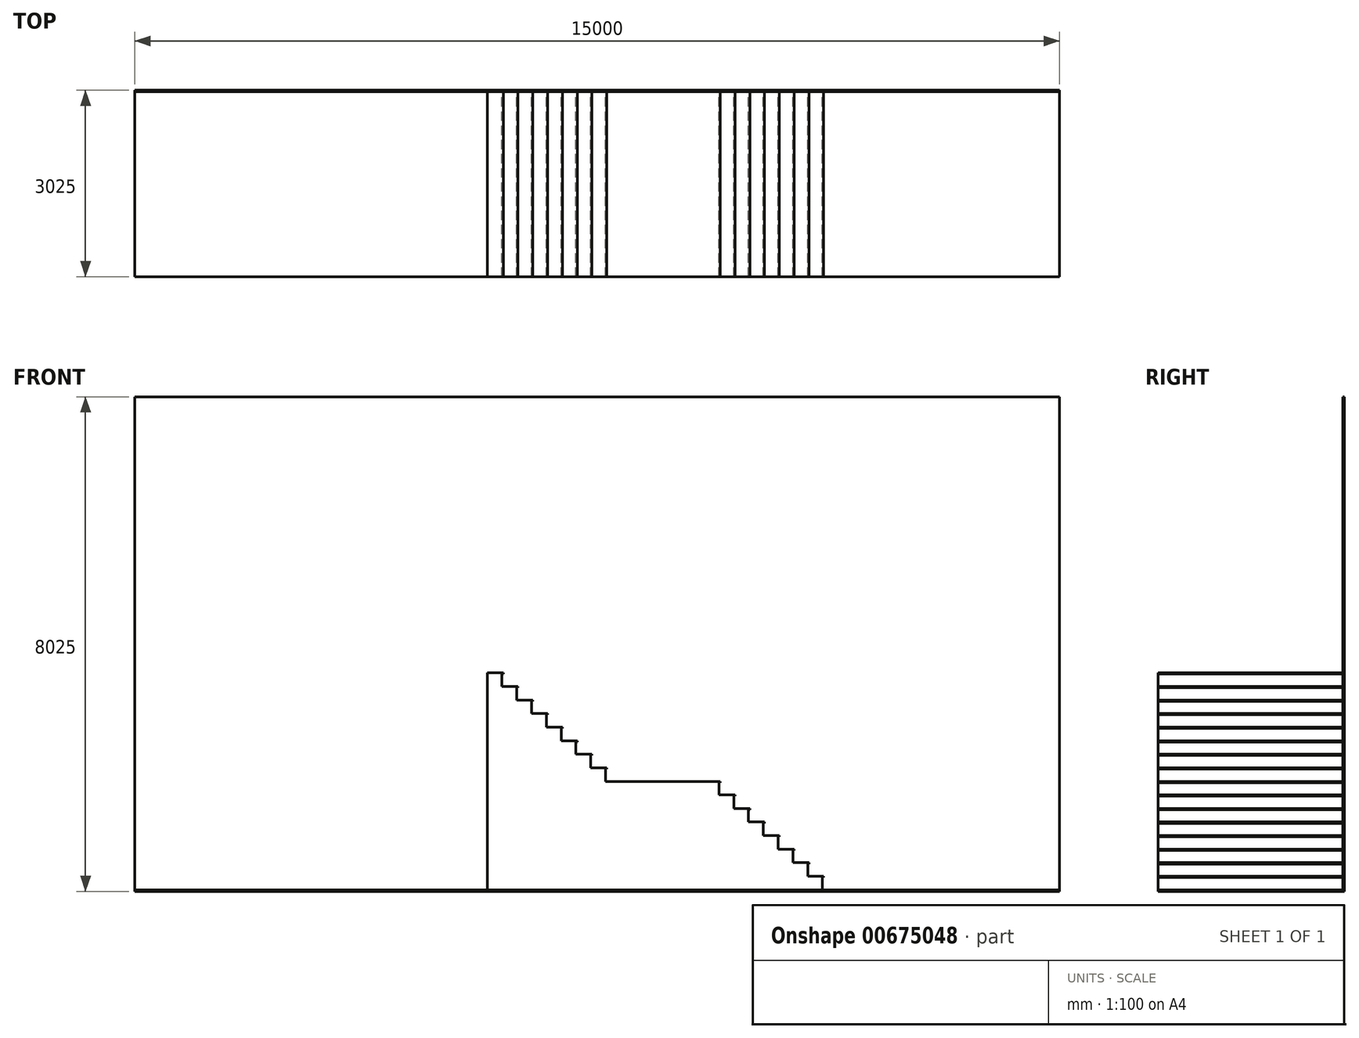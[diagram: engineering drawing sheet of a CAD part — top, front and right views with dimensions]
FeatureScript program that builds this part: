
annotation { "Feature Type Name" : "Feature", "Feature Type Description" : "" }
export const myFeature = defineFeature(function(context is Context, id is Id, definition is map)
    precondition{}
    {
        {
            var Q0;
            Q0=qCreatedBy(makeId("Front.planeOp"),FACE);
            var sketch = newSketch(context, id + "F0", { "sketchPlane" : qUnion([Q0])});
            skLineSegment(sketch, "E0", {"start": v(0, 0) * mm, "end": v(260, 0) * mm});
            skLineSegment(sketch, "E1", {"start": v(260, 0) * mm, "end": v(260, -20) * mm});
            skLineSegment(sketch, "E2", {"start": v(260, -20) * mm, "end": v(240, -20) * mm});
            skLineSegment(sketch, "E3", {"start": v(240, -20) * mm, "end": v(240, -220) * mm});
            skPoint(sketch, "E4.orphan", {"position": v(260, -220) * mm});
            skLineSegment(sketch, "E5", {"start": v(0, 0) * mm, "end": v(240, -220) * mm, "construction": true});
            skLineSegment(sketch, "E6", {"start": v(240, -220) * mm, "end": v(500, -220) * mm});
            skLineSegment(sketch, "E7", {"start": v(500, -220) * mm, "end": v(500, -240) * mm});
            skLineSegment(sketch, "E8", {"start": v(500, -240) * mm, "end": v(480, -240) * mm});
            skLineSegment(sketch, "E9", {"start": v(480, -240) * mm, "end": v(480, -440) * mm});
            skPoint(sketch, "E10.orphan", {"position": v(500, -440) * mm});
            skLineSegment(sketch, "E11", {"start": v(240, -220) * mm, "end": v(480, -440) * mm, "construction": true});
            skLineSegment(sketch, "E12", {"start": v(480, -440) * mm, "end": v(740, -440) * mm});
            skLineSegment(sketch, "E13", {"start": v(740, -440) * mm, "end": v(740, -460) * mm});
            skLineSegment(sketch, "E14", {"start": v(740, -460) * mm, "end": v(720, -460) * mm});
            skLineSegment(sketch, "E15", {"start": v(720, -460) * mm, "end": v(720, -660) * mm});
            skPoint(sketch, "E16.orphan", {"position": v(740, -660) * mm});
            skLineSegment(sketch, "E17", {"start": v(480, -440) * mm, "end": v(720, -660) * mm, "construction": true});
            skLineSegment(sketch, "E18", {"start": v(720, -660) * mm, "end": v(980, -660) * mm});
            skLineSegment(sketch, "E19", {"start": v(980, -660) * mm, "end": v(980, -680) * mm});
            skLineSegment(sketch, "E20", {"start": v(980, -680) * mm, "end": v(960, -680) * mm});
            skLineSegment(sketch, "E21", {"start": v(960, -680) * mm, "end": v(960, -880) * mm});
            skPoint(sketch, "E22.orphan", {"position": v(980, -880) * mm});
            skLineSegment(sketch, "E23", {"start": v(720, -660) * mm, "end": v(960, -880) * mm, "construction": true});
            skLineSegment(sketch, "E24", {"start": v(960, -880) * mm, "end": v(1220, -880) * mm});
            skLineSegment(sketch, "E25", {"start": v(1220, -880) * mm, "end": v(1220, -900) * mm});
            skLineSegment(sketch, "E26", {"start": v(1220, -900) * mm, "end": v(1200, -900) * mm});
            skLineSegment(sketch, "E27", {"start": v(1200, -900) * mm, "end": v(1200, -1100) * mm});
            skPoint(sketch, "E28.orphan", {"position": v(1220, -1100) * mm});
            skLineSegment(sketch, "E29", {"start": v(960, -880) * mm, "end": v(1200, -1100) * mm, "construction": true});
            skLineSegment(sketch, "E30", {"start": v(1200, -1100) * mm, "end": v(1460, -1100) * mm});
            skLineSegment(sketch, "E31", {"start": v(1460, -1100) * mm, "end": v(1460, -1120) * mm});
            skLineSegment(sketch, "E32", {"start": v(1460, -1120) * mm, "end": v(1440, -1120) * mm});
            skLineSegment(sketch, "E33", {"start": v(1440, -1120) * mm, "end": v(1440, -1320) * mm});
            skPoint(sketch, "E34.orphan", {"position": v(1460, -1320) * mm});
            skLineSegment(sketch, "E35", {"start": v(1200, -1100) * mm, "end": v(1440, -1320) * mm, "construction": true});
            skLineSegment(sketch, "E36", {"start": v(1440, -1320) * mm, "end": v(1700, -1320) * mm});
            skLineSegment(sketch, "E37", {"start": v(1700, -1320) * mm, "end": v(1700, -1340) * mm});
            skLineSegment(sketch, "E38", {"start": v(1700, -1340) * mm, "end": v(1680, -1340) * mm});
            skLineSegment(sketch, "E39", {"start": v(1680, -1340) * mm, "end": v(1680, -1540) * mm});
            skPoint(sketch, "E40.orphan", {"position": v(1700, -1540) * mm});
            skLineSegment(sketch, "E41", {"start": v(1440, -1320) * mm, "end": v(1680, -1540) * mm, "construction": true});
            skLineSegment(sketch, "E42", {"start": v(1680, -1540) * mm, "end": v(1940, -1540) * mm});
            skLineSegment(sketch, "E43", {"start": v(1940, -1540) * mm, "end": v(1940, -1560) * mm});
            skLineSegment(sketch, "E44", {"start": v(1940, -1560) * mm, "end": v(1920, -1560) * mm});
            skLineSegment(sketch, "E45", {"start": v(1920, -1560) * mm, "end": v(1920, -1760) * mm});
            skPoint(sketch, "E46.orphan", {"position": v(1940, -1760) * mm});
            skLineSegment(sketch, "E47", {"start": v(1680, -1540) * mm, "end": v(1920, -1760) * mm, "construction": true});
            skLineSegment(sketch, "E48", {"start": v(1920, -1760) * mm, "end": v(3520, -1760) * mm});
            skLineSegment(sketch, "E49", {"start": v(3520, -1760) * mm, "end": v(3780, -1760) * mm});
            skLineSegment(sketch, "E50", {"start": v(3780, -1760) * mm, "end": v(3780, -1780) * mm});
            skLineSegment(sketch, "E51", {"start": v(3780, -1780) * mm, "end": v(3760, -1780) * mm});
            skLineSegment(sketch, "E52", {"start": v(3760, -1780) * mm, "end": v(3760, -1980) * mm});
            skPoint(sketch, "E53.orphan", {"position": v(3780, -1980) * mm});
            skLineSegment(sketch, "E54", {"start": v(3520, -1760) * mm, "end": v(3760, -1980) * mm, "construction": true});
            skLineSegment(sketch, "E55", {"start": v(3760, -1980) * mm, "end": v(4020, -1980) * mm});
            skLineSegment(sketch, "E56", {"start": v(4020, -1980) * mm, "end": v(4020, -2000) * mm});
            skLineSegment(sketch, "E57", {"start": v(4020, -2000) * mm, "end": v(4000, -2000) * mm});
            skLineSegment(sketch, "E58", {"start": v(4000, -2000) * mm, "end": v(4000, -2200) * mm});
            skPoint(sketch, "E59.orphan", {"position": v(4020, -2200) * mm});
            skLineSegment(sketch, "E60", {"start": v(3760, -1980) * mm, "end": v(4000, -2200) * mm, "construction": true});
            skLineSegment(sketch, "E61", {"start": v(4000, -2200) * mm, "end": v(4260, -2200) * mm});
            skLineSegment(sketch, "E62", {"start": v(4260, -2200) * mm, "end": v(4260, -2220) * mm});
            skLineSegment(sketch, "E63", {"start": v(4260, -2220) * mm, "end": v(4240, -2220) * mm});
            skLineSegment(sketch, "E64", {"start": v(4240, -2220) * mm, "end": v(4240, -2420) * mm});
            skPoint(sketch, "E65.orphan", {"position": v(4260, -2420) * mm});
            skLineSegment(sketch, "E66", {"start": v(4000, -2200) * mm, "end": v(4240, -2420) * mm, "construction": true});
            skLineSegment(sketch, "E67", {"start": v(4240, -2420) * mm, "end": v(4500, -2420) * mm});
            skLineSegment(sketch, "E68", {"start": v(4500, -2420) * mm, "end": v(4500, -2440) * mm});
            skLineSegment(sketch, "E69", {"start": v(4500, -2440) * mm, "end": v(4480, -2440) * mm});
            skLineSegment(sketch, "E70", {"start": v(4480, -2440) * mm, "end": v(4480, -2640) * mm});
            skPoint(sketch, "E71.orphan", {"position": v(4500, -2640) * mm});
            skLineSegment(sketch, "E72", {"start": v(4240, -2420) * mm, "end": v(4480, -2640) * mm, "construction": true});
            skLineSegment(sketch, "E73", {"start": v(4480, -2640) * mm, "end": v(4740, -2640) * mm});
            skLineSegment(sketch, "E74", {"start": v(4740, -2640) * mm, "end": v(4740, -2660) * mm});
            skLineSegment(sketch, "E75", {"start": v(4740, -2660) * mm, "end": v(4720, -2660) * mm});
            skLineSegment(sketch, "E76", {"start": v(4720, -2660) * mm, "end": v(4720, -2860) * mm});
            skPoint(sketch, "E77.orphan", {"position": v(4740, -2860) * mm});
            skLineSegment(sketch, "E78", {"start": v(4480, -2640) * mm, "end": v(4720, -2860) * mm, "construction": true});
            skLineSegment(sketch, "E79", {"start": v(4720, -2860) * mm, "end": v(4980, -2860) * mm});
            skLineSegment(sketch, "E80", {"start": v(4980, -2860) * mm, "end": v(4980, -2880) * mm});
            skLineSegment(sketch, "E81", {"start": v(4980, -2880) * mm, "end": v(4960, -2880) * mm});
            skLineSegment(sketch, "E82", {"start": v(4960, -2880) * mm, "end": v(4960, -3080) * mm});
            skPoint(sketch, "E83.orphan", {"position": v(4980, -3080) * mm});
            skLineSegment(sketch, "E84", {"start": v(4720, -2860) * mm, "end": v(4960, -3080) * mm, "construction": true});
            skLineSegment(sketch, "E85", {"start": v(4960, -3080) * mm, "end": v(5220, -3080) * mm});
            skLineSegment(sketch, "E86", {"start": v(5220, -3080) * mm, "end": v(5220, -3100) * mm});
            skLineSegment(sketch, "E87", {"start": v(5220, -3100) * mm, "end": v(5200, -3100) * mm});
            skLineSegment(sketch, "E88", {"start": v(5200, -3100) * mm, "end": v(5200, -3300) * mm});
            skPoint(sketch, "E89.orphan", {"position": v(5220, -3300) * mm});
            skLineSegment(sketch, "E90", {"start": v(4960, -3080) * mm, "end": v(5200, -3300) * mm, "construction": true});
            skLineSegment(sketch, "E91", {"start": v(5200, -3300) * mm, "end": v(5460, -3300) * mm});
            skLineSegment(sketch, "E92", {"start": v(5460, -3300) * mm, "end": v(5460, -3320) * mm});
            skLineSegment(sketch, "E93", {"start": v(5460, -3320) * mm, "end": v(5440, -3320) * mm});
            skLineSegment(sketch, "E94", {"start": v(5440, -3320) * mm, "end": v(5440, -3520) * mm});
            skPoint(sketch, "E95.orphan", {"position": v(5460, -3520) * mm});
            skLineSegment(sketch, "E96", {"start": v(5200, -3300) * mm, "end": v(5440, -3520) * mm, "construction": true});
            skLineSegment(sketch, "E97", {"start": v(0, 0) * mm, "end": v(0, -3520) * mm});
            skLineSegment(sketch, "E98", {"start": v(0, -3520) * mm, "end": v(5440, -3520) * mm});
            skSolve(sketch);
        }
        {
            var Q0;
            Q0 = qSketchRegion(id + "F0", true);
            extrude(context, id + "F1", {"entities" : qUnion([Q0]), "depth" : 3000 * mm, "offsetDistance" : 25 * mm});
        }
        {
            var Q0;
            Q0=makeQuery(id+"F1.opExtrude","CAP_FACE",FACE,{"disambiguationData":[OSD([sQuery(id+"F0.wireOp",EDGE,"E0"),sQuery(id+"F0.wireOp",EDGE,"E1"),sQuery(id+"F0.wireOp",EDGE,"E2"),sQuery(id+"F0.wireOp",EDGE,"E3"),sQuery(id+"F0.wireOp",EDGE,"E6"),sQuery(id+"F0.wireOp",EDGE,"E7"),sQuery(id+"F0.wireOp",EDGE,"E8"),sQuery(id+"F0.wireOp",EDGE,"E9"),sQuery(id+"F0.wireOp",EDGE,"E12"),sQuery(id+"F0.wireOp",EDGE,"E13"),sQuery(id+"F0.wireOp",EDGE,"E14"),sQuery(id+"F0.wireOp",EDGE,"E15"),sQuery(id+"F0.wireOp",EDGE,"E18"),sQuery(id+"F0.wireOp",EDGE,"E19"),sQuery(id+"F0.wireOp",EDGE,"E20"),sQuery(id+"F0.wireOp",EDGE,"E21"),sQuery(id+"F0.wireOp",EDGE,"E24"),sQuery(id+"F0.wireOp",EDGE,"E25"),sQuery(id+"F0.wireOp",EDGE,"E26"),sQuery(id+"F0.wireOp",EDGE,"E27"),sQuery(id+"F0.wireOp",EDGE,"E30"),sQuery(id+"F0.wireOp",EDGE,"E31"),sQuery(id+"F0.wireOp",EDGE,"E32"),sQuery(id+"F0.wireOp",EDGE,"E33"),sQuery(id+"F0.wireOp",EDGE,"E36"),sQuery(id+"F0.wireOp",EDGE,"E37"),sQuery(id+"F0.wireOp",EDGE,"E38"),sQuery(id+"F0.wireOp",EDGE,"E39"),sQuery(id+"F0.wireOp",EDGE,"E42"),sQuery(id+"F0.wireOp",EDGE,"E43"),sQuery(id+"F0.wireOp",EDGE,"E44"),sQuery(id+"F0.wireOp",EDGE,"E45"),sQuery(id+"F0.wireOp",EDGE,"E48"),sQuery(id+"F0.wireOp",EDGE,"E49"),sQuery(id+"F0.wireOp",EDGE,"E50"),sQuery(id+"F0.wireOp",EDGE,"E51"),sQuery(id+"F0.wireOp",EDGE,"E52"),sQuery(id+"F0.wireOp",EDGE,"E55"),sQuery(id+"F0.wireOp",EDGE,"E56"),sQuery(id+"F0.wireOp",EDGE,"E57"),sQuery(id+"F0.wireOp",EDGE,"E58"),sQuery(id+"F0.wireOp",EDGE,"E61"),sQuery(id+"F0.wireOp",EDGE,"E62"),sQuery(id+"F0.wireOp",EDGE,"E63"),sQuery(id+"F0.wireOp",EDGE,"E64"),sQuery(id+"F0.wireOp",EDGE,"E67"),sQuery(id+"F0.wireOp",EDGE,"E68"),sQuery(id+"F0.wireOp",EDGE,"E69"),sQuery(id+"F0.wireOp",EDGE,"E70"),sQuery(id+"F0.wireOp",EDGE,"E73"),sQuery(id+"F0.wireOp",EDGE,"E74"),sQuery(id+"F0.wireOp",EDGE,"E75"),sQuery(id+"F0.wireOp",EDGE,"E76"),sQuery(id+"F0.wireOp",EDGE,"E79"),sQuery(id+"F0.wireOp",EDGE,"E80"),sQuery(id+"F0.wireOp",EDGE,"E81"),sQuery(id+"F0.wireOp",EDGE,"E82"),sQuery(id+"F0.wireOp",EDGE,"E85"),sQuery(id+"F0.wireOp",EDGE,"E86"),sQuery(id+"F0.wireOp",EDGE,"E87"),sQuery(id+"F0.wireOp",EDGE,"E88"),sQuery(id+"F0.wireOp",EDGE,"E91"),sQuery(id+"F0.wireOp",EDGE,"E92"),sQuery(id+"F0.wireOp",EDGE,"E93"),sQuery(id+"F0.wireOp",EDGE,"E94"),sQuery(id+"F0.wireOp",EDGE,"E97"),sQuery(id+"F0.wireOp",EDGE,"E98")])],"isStart":true});
            var sketch = newSketch(context, id + "F2", { "sketchPlane" : qUnion([Q0])});
            skLineSegment(sketch, "E99.bottom", {"start": v(5716.77, -3520) * mm, "end": v(-9283.23, -3520) * mm});
            skLineSegment(sketch, "E99.top", {"start": v(5716.77, 4480) * mm, "end": v(-9283.23, 4480) * mm});
            skLineSegment(sketch, "E99.left", {"start": v(5716.77, -3520) * mm, "end": v(5716.77, 4480) * mm});
            skLineSegment(sketch, "E99.right", {"start": v(-9283.23, -3520) * mm, "end": v(-9283.23, 4480) * mm});
            skSolve(sketch);
        }
        {
            var Q0;
            Q0 = qSketchRegion(id + "F2", true);
            extrude(context, id + "F3", {"entities" : qUnion([Q0]), "depth" : 25 * mm, "offsetDistance" : 25 * mm});
        }
        {
            var Q0;
            Q0=makeQuery(id+"F1.opExtrude","SWEPT_FACE",FACE,{"disambiguationData":[OSD([sQuery(id+"F0.wireOp",EDGE,"E98")])]});
            var sketch = newSketch(context, id + "F4", { "sketchPlane" : qUnion([Q0])});
            skPoint(sketch, "E100.0", {"position": v(-5716.77, -25) * mm});
            skLineSegment(sketch, "E101.bottom", {"start": v(-5716.77, -25) * mm, "end": v(9283.23, -25) * mm});
            skLineSegment(sketch, "E101.top", {"start": v(-5716.77, 3000) * mm, "end": v(9283.23, 3000) * mm});
            skLineSegment(sketch, "E101.left", {"start": v(-5716.77, -25) * mm, "end": v(-5716.77, 3000) * mm});
            skLineSegment(sketch, "E101.right", {"start": v(9283.23, -25) * mm, "end": v(9283.23, 3000) * mm});
            skSolve(sketch);
        }
        {
            var Q0;
            Q0 = qSketchRegion(id + "F4", true);
            extrude(context, id + "F5", {"entities" : qUnion([Q0]), "depth" : 25 * mm, "offsetDistance" : 25 * mm});
        }
    });
